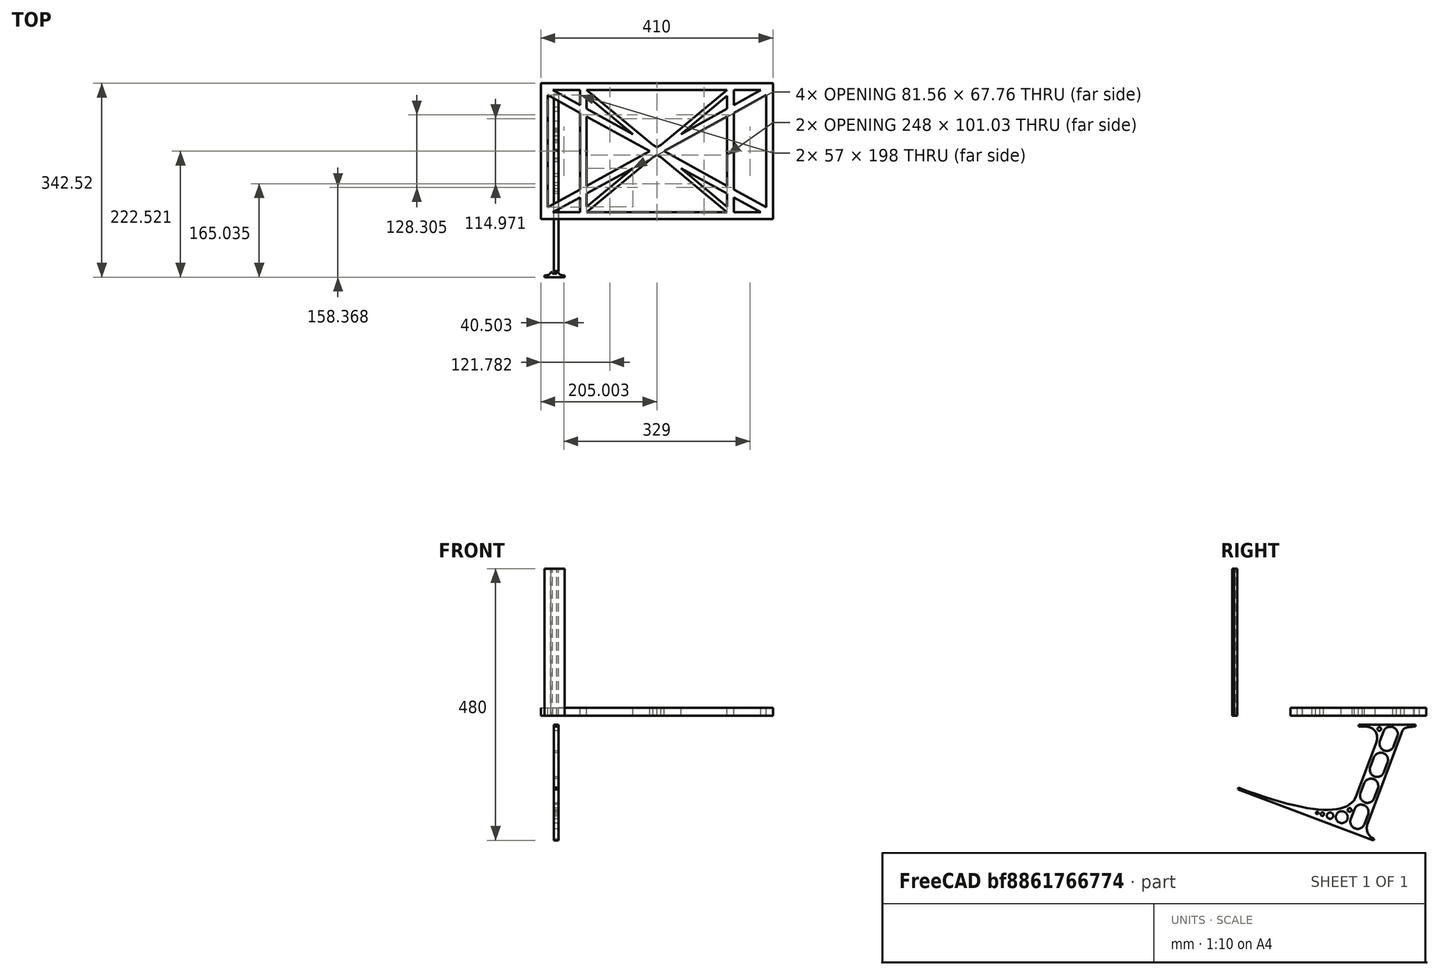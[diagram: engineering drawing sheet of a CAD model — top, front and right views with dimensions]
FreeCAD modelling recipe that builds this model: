
FCSTD DOCUMENT  (FreeCAD 0.19R0.19.2)
Label: laptopStand053
License: All rights reserved
LicenseURL: http://en.wikipedia.org/wiki/All_rights_reserved
objects: Sketcher::SketchObject×3, Part::Extrusion×3
note: 6 computed .brp shape members not serialized (recipe doc carries the construction recipe); baked Part::Feature solids carry a one-line shape summary decoded from their .brp

FEATURE [Sketcher::SketchObject] Sketch
  FullyConstrained = true
  sketch-geometry (92):
    g0: LineSegment StartX=-22.9272 StartY=136.221 StartZ=0 EndX=387.073 EndY=136.221 EndZ=0
    g1: LineSegment StartX=-22.9272 StartY=-103.779 StartZ=0 EndX=387.073 EndY=-103.779 EndZ=0
    g2: LineSegment StartX=375.073 StartY=115.221 StartZ=0 EndX=318.073 EndY=83.9235 EndZ=0
    g3: LineSegment StartX=-10.9272 StartY=-82.7794 StartZ=0 EndX=46.0728 EndY=-51.4823 EndZ=0
    g4: LineSegment StartX=-1.92719 StartY=124.221 StartZ=0 EndX=46.0728 EndY=97.8651 EndZ=0
    g5: LineSegment StartX=366.073 StartY=-91.7794 StartZ=0 EndX=318.073 EndY=-65.424 EndZ=0
    g6: LineSegment StartX=-10.9272 StartY=115.221 StartZ=0 EndX=-10.9272 EndY=-82.7794 EndZ=0
    g7: LineSegment StartX=375.073 StartY=-82.7794 StartZ=0 EndX=375.073 EndY=115.221 EndZ=0
    g8: LineSegment StartX=-1.92719 StartY=-91.7794 StartZ=0 EndX=46.0728 EndY=-91.7794 EndZ=0
    g9: LineSegment StartX=318.073 StartY=124.221 StartZ=0 EndX=366.073 EndY=124.221 EndZ=0
    g10: LineSegment StartX=306.073 StartY=-81.8102 StartZ=0 EndX=224.513 EndY=-14.0532 EndZ=0
    g11: LineSegment StartX=58.0728 StartY=114.251 StartZ=0 EndX=139.632 EndY=46.4944 EndZ=0
    g12: LineSegment StartX=306.073 StartY=124.221 StartZ=0 EndX=189.124 EndY=27.0628 EndZ=0
    g13: LineSegment StartX=58.0728 StartY=-91.7794 StartZ=0 EndX=175.022 EndY=5.37834 EndZ=0
    g14: LineSegment StartX=46.0728 StartY=124.221 StartZ=0 EndX=46.0728 EndY=97.8651 EndZ=0
    g15: LineSegment StartX=58.0728 StartY=-81.8102 StartZ=0 EndX=58.0728 EndY=-58.8351 EndZ=0
    g16: LineSegment StartX=318.073 StartY=124.221 StartZ=0 EndX=318.073 EndY=97.8651 EndZ=0
    g17: LineSegment StartX=306.073 StartY=114.251 StartZ=0 EndX=306.073 EndY=91.2763 EndZ=0
    g18: LineSegment StartX=224.513 StartY=46.4944 StartZ=0 EndX=306.073 EndY=114.251 EndZ=0
    g19: LineSegment StartX=175.022 StartY=27.0628 StartZ=0 EndX=58.0728 EndY=124.221 EndZ=0
    g20: LineSegment StartX=169.377 StartY=16.2206 StartZ=0 EndX=58.0728 EndY=77.3346 EndZ=0
    g21: LineSegment StartX=139.632 StartY=-14.0532 StartZ=0 EndX=58.0728 EndY=-81.8102 EndZ=0
    g22: LineSegment StartX=194.768 StartY=16.2206 StartZ=0 EndX=306.073 EndY=-44.8935 EndZ=0
    g23: LineSegment StartX=224.513 StartY=46.4944 StartZ=0 EndX=306.073 EndY=91.2763 EndZ=0
    g24: LineSegment StartX=139.632 StartY=-14.0532 StartZ=0 EndX=58.0728 EndY=-58.8351 EndZ=0
    g25: LineSegment StartX=189.124 StartY=5.37834 StartZ=0 EndX=306.073 EndY=-91.7794 EndZ=0
    g26: LineSegment StartX=306.073 StartY=77.3346 StartZ=0 EndX=306.073 EndY=-44.8935 EndZ=0
    g27: LineSegment StartX=318.073 StartY=83.9235 StartZ=0 EndX=318.073 EndY=-51.4823 EndZ=0
    g28: LineSegment StartX=318.073 StartY=97.8651 StartZ=0 EndX=366.073 EndY=124.221 EndZ=0
    g29: LineSegment StartX=306.073 StartY=77.3346 StartZ=0 EndX=194.768 EndY=16.2206 EndZ=0
    g30: LineSegment StartX=306.073 StartY=-58.8351 StartZ=0 EndX=224.513 EndY=-14.0532 EndZ=0
    g31: LineSegment StartX=306.073 StartY=-58.8351 StartZ=0 EndX=306.073 EndY=-81.8102 EndZ=0
    g32: LineSegment StartX=318.073 StartY=-51.4823 StartZ=0 EndX=375.073 EndY=-82.7794 EndZ=0
    g33: LineSegment StartX=318.073 StartY=-65.424 StartZ=0 EndX=318.073 EndY=-91.7794 EndZ=0
    g34: LineSegment StartX=318.073 StartY=-91.7794 StartZ=0 EndX=366.073 EndY=-91.7794 EndZ=0
    g35: LineSegment StartX=58.0728 StartY=-44.8935 StartZ=0 EndX=58.0728 EndY=77.3346 EndZ=0
    g36: LineSegment StartX=46.0728 StartY=-65.424 StartZ=0 EndX=-1.92719 EndY=-91.7794 EndZ=0
    g37: LineSegment StartX=46.0728 StartY=-65.424 StartZ=0 EndX=46.0728 EndY=-91.7794 EndZ=0
    g38: LineSegment StartX=58.0728 StartY=-44.8935 StartZ=0 EndX=169.377 EndY=16.2206 EndZ=0
    g39: LineSegment StartX=58.0728 StartY=91.2763 StartZ=0 EndX=58.0728 EndY=114.251 EndZ=0
    g40: LineSegment StartX=46.0728 StartY=83.9235 StartZ=0 EndX=46.0728 EndY=-51.4823 EndZ=0
    g41: LineSegment StartX=46.0728 StartY=124.221 StartZ=0 EndX=-1.92719 EndY=124.221 EndZ=0
    g42: LineSegment StartX=58.0728 StartY=91.2763 StartZ=0 EndX=139.632 EndY=46.4944 EndZ=0
    g43: LineSegment StartX=46.0728 StartY=83.9235 StartZ=0 EndX=-10.9272 EndY=115.221 EndZ=0
    g44: LineSegment StartX=-22.9272 StartY=136.221 StartZ=0 EndX=-42.9272 EndY=136.221 EndZ=0
    g45: LineSegment StartX=387.073 StartY=136.221 StartZ=0 EndX=407.073 EndY=136.221 EndZ=0
    g46: LineSegment StartX=-42.9272 StartY=136.221 StartZ=0 EndX=-42.9272 EndY=-103.779 EndZ=0
    g47: LineSegment StartX=-22.9272 StartY=-103.779 StartZ=0 EndX=-42.9272 EndY=-103.779 EndZ=0
    g48: LineSegment StartX=407.073 StartY=136.221 StartZ=0 EndX=407.073 EndY=-103.779 EndZ=0
    g49: LineSegment StartX=387.073 StartY=-103.779 StartZ=0 EndX=407.073 EndY=-103.779 EndZ=0
    g50: LineSegment StartX=179.022 StartY=27.0628 StartZ=0 EndX=179.022 EndY=124.221 EndZ=0
    g51: LineSegment StartX=185.124 StartY=27.0628 StartZ=0 EndX=185.124 EndY=124.221 EndZ=0
    g52: ArcOfCircle CenterX=-26.9272 CenterY=22.1087 CenterZ=0 NormalX=0 NormalY=0 NormalZ=1 AngleXU=0 Radius=8 StartAngle=1e-16 EndAngle=3.14159
    g53: ArcOfCircle CenterX=-26.9272 CenterY=-83.7794 CenterZ=0 NormalX=0 NormalY=0 NormalZ=1 AngleXU=0 Radius=8 StartAngle=3.14159 EndAngle=6.28319
    g54: LineSegment StartX=-34.9272 StartY=22.1087 StartZ=0 EndX=-34.9272 EndY=-83.7794 EndZ=0
    g55: LineSegment StartX=-18.9272 StartY=22.1087 StartZ=0 EndX=-18.9272 EndY=-83.7794 EndZ=0
    g56: LineSegment StartX=185.124 StartY=-91.7794 StartZ=0 EndX=306.073 EndY=-91.7794 EndZ=0
    g57: LineSegment StartX=179.022 StartY=-91.7794 StartZ=0 EndX=58.0728 EndY=-91.7794 EndZ=0
    g58: LineSegment StartX=306.073 StartY=124.221 StartZ=0 EndX=185.124 EndY=124.221 EndZ=0
    g59: LineSegment StartX=179.022 StartY=124.221 StartZ=0 EndX=58.0728 EndY=124.221 EndZ=0
    g60: ArcOfCircle CenterX=391.073 CenterY=22.1087 CenterZ=0 NormalX=0 NormalY=0 NormalZ=1 AngleXU=0 Radius=8 StartAngle=-4.4e-15 EndAngle=3.14159
    g61: LineSegment StartX=399.073 StartY=22.1087 StartZ=0 EndX=399.073 EndY=-83.7794 EndZ=0
    g62: LineSegment StartX=383.073 StartY=22.1087 StartZ=0 EndX=383.073 EndY=-83.7794 EndZ=0
    g63: ArcOfCircle CenterX=391.073 CenterY=-83.7794 CenterZ=0 NormalX=0 NormalY=0 NormalZ=1 AngleXU=0 Radius=8 StartAngle=3.14159 EndAngle=6.28319
    g64: Circle CenterX=175.022 CenterY=27.0628 CenterZ=0 NormalX=0 NormalY=0 NormalZ=1 AngleXU=0 Radius=1
    g65: Circle CenterX=179.022 CenterY=24.8665 CenterZ=0 NormalX=0 NormalY=0 NormalZ=1 AngleXU=0 Radius=1
    g66: Circle CenterX=179.022 CenterY=27.0628 CenterZ=0 NormalX=0 NormalY=0 NormalZ=1 AngleXU=0 Radius=1
    g67: BSplineCurve PolesCount=3 KnotsCount=2 Degree=2 IsPeriodic=0
    g68: GeomPoint X=175.022 Y=27.0628 Z=0
    g69: GeomPoint X=179.022 Y=27.0628 Z=0
    g70: Circle CenterX=189.124 CenterY=27.0628 CenterZ=0 NormalX=0 NormalY=0 NormalZ=1 AngleXU=0 Radius=1
    g71: Circle CenterX=185.124 CenterY=24.8665 CenterZ=0 NormalX=0 NormalY=0 NormalZ=1 AngleXU=0 Radius=1
    g72: Circle CenterX=185.124 CenterY=27.0628 CenterZ=0 NormalX=0 NormalY=0 NormalZ=1 AngleXU=0 Radius=1
    g73: BSplineCurve PolesCount=3 KnotsCount=2 Degree=2 IsPeriodic=0
    g74: GeomPoint X=189.124 Y=27.0628 Z=0
    g75: GeomPoint X=185.124 Y=27.0628 Z=0
    g76: Circle CenterX=175.022 CenterY=5.37834 CenterZ=0 NormalX=0 NormalY=0 NormalZ=1 AngleXU=0 Radius=1
    g77: Circle CenterX=179.022 CenterY=7.57463 CenterZ=0 NormalX=0 NormalY=0 NormalZ=1 AngleXU=0 Radius=1
    g78: Circle CenterX=179.022 CenterY=5.34704 CenterZ=0 NormalX=0 NormalY=0 NormalZ=1 AngleXU=0 Radius=1
    g79: BSplineCurve PolesCount=3 KnotsCount=2 Degree=2 IsPeriodic=0
    g80: GeomPoint X=175.022 Y=5.37834 Z=0
    g81: GeomPoint X=179.022 Y=5.34704 Z=0
    g82: Circle CenterX=189.124 CenterY=5.37834 CenterZ=0 NormalX=0 NormalY=0 NormalZ=1 AngleXU=0 Radius=1
    g83: Circle CenterX=185.124 CenterY=7.57463 CenterZ=0 NormalX=0 NormalY=0 NormalZ=1 AngleXU=0 Radius=1
    g84: Circle CenterX=185.124 CenterY=5.34704 CenterZ=0 NormalX=0 NormalY=0 NormalZ=1 AngleXU=0 Radius=1
    g85: BSplineCurve PolesCount=3 KnotsCount=2 Degree=2 IsPeriodic=0
    g86: GeomPoint X=189.124 Y=5.37834 Z=0
    g87: GeomPoint X=185.124 Y=5.34704 Z=0
    g88: LineSegment StartX=179.022 StartY=5.34704 StartZ=0 EndX=179.022 EndY=-91.7794 EndZ=0
    g89: LineSegment StartX=185.124 StartY=-91.7794 StartZ=0 EndX=185.124 EndY=5.34704 EndZ=0
    g90: LineSegment StartX=179.022 StartY=124.221 StartZ=0 EndX=177.022 EndY=124.221 EndZ=0
    g91: LineSegment StartX=179.022 StartY=124.221 StartZ=0 EndX=179.022 EndY=122.221 EndZ=0
  constraints (183):
    c: Horizontal(g0)
    c: Distance(g0) = 410
    c: Horizontal(g1)
    c: Block(g0)
    c: Horizontal(g8)
    c: Horizontal(g9)
    c: Tangent(g5,g20)
    c: PointOnObject(g20,g3)
    c: PointOnObject(g22,g2)
    c: Coincident(g42,g11)
    c: Coincident(g18,g23)
    c: Coincident(g24,g21)
    c: Coincident(g30,g10)
    c: Coincident(g18,g17)
    c: Tangent(g17,g26)
    c: Tangent(g16,g27)
    c: Coincident(g23,g17)
    c: Tangent(g23,g28)
    c: Coincident(g2,g27)
    c: Coincident(g29,g26)
    c: Tangent(g2,g29)
    c: Coincident(g31,g10)
    c: Tangent(g5,g30)
    c: Tangent(g26,g31)
    c: Coincident(g22,g26)
    c: Tangent(g22,g32)
    c: Coincident(g27,g32)
    c: Coincident(g33,g5)
    c: Tangent(g27,g33)
    c: Coincident(g21,g15)
    c: Tangent(g15,g35)
    c: Coincident(g24,g15)
    c: Tangent(g24,g36)
    c: Coincident(g37,g36)
    c: Tangent(g14,g37)
    c: Coincident(g3,g40)
    c: Coincident(g38,g35)
    c: Tangent(g3,g38)
    c: Tangent(g35,g39)
    c: Tangent(g14,g40)
    c: Coincident(g11,g39)
    c: Coincident(g4,g14)
    c: Coincident(g42,g39)
    c: Tangent(g4,g42)
    c: Coincident(g20,g35)
    c: Coincident(g43,g40)
    c: Tangent(g20,g43)
    c: Block(g19)
    c: Block(g12)
    c: Block(g16)
    c: Block(g28)
    c: Block(g2)
    c: Block(g32)
    c: Block(g7)
    c: Block(g30)
    c: Block(g31)
    c: Block(g5)
    c: Block(g33)
    c: Block(g18)
    c: Block(g25)
    c: Block(g13)
    c: Block(g24)
    c: Block(g21)
    c: Block(g37)
    c: Block(g36)
    c: Block(g3)
    c: Block(g6)
    c: Block(g43)
    c: Block(g4)
    c: Block(g14)
    c: Block(g11)
    c: Block(g39)
    c: Block(g29)
    c: Block(g26)
    c: Block(g20)
    c: Block(g38)
    c: Block(g41)
    c: Block(g9)
    c: Block(g34)
    c: Block(g8)
    c: Horizontal(g44)
    c: Distance(g44) = 20
    c: Coincident(g45,g0)
    c: Horizontal(g45)
    c: Distance(g45) = 20
    c: Coincident(g46,g44)
    c: Vertical(g46)
    c: Horizontal(g47)
    c: Coincident(g47,g46)
    c: Coincident(g48,g45)
    c: Vertical(g48)
    c: Coincident(g49,g1)
    c: Horizontal(g49)
    c: Coincident(g49,g48)
    c: Block(g48)
    c: Block(g47)
    c: Block(g46)
    c: Block(g1)
    c: Vertical(g50)
    c: Vertical(g51)
    c: Block(g50)
    c: Block(g51)
    c: Tangent(g52,g55) = 1.5708
    c: Tangent(g52,g54) = -1.5708
    c: Tangent(g54,g53) = -1.5708
    c: Tangent(g55,g53) = 1.5708
    c: Vertical(g54)
    c: Equal(g52,g53)
    c: Block(g55)
    c: Block(g54)
    c: Coincident(g56,g25)
    c: Horizontal(g56)
    c: Coincident(g57,g13)
    c: Horizontal(g57)
    c: Coincident(g58,g12)
    c: Coincident(g58,g51)
    c: Horizontal(g58)
    c: Coincident(g59,g50)
    c: Coincident(g59,g19)
    c: Horizontal(g59)
    c: Distance(g49) = 20
    c: Distance(g1) = 410
    c: Tangent(g60,g61) = 1.5708
    c: Tangent(g61,g63) = 1.5708
    c: Equal(g60,g63)
    c: Coincident(g62,g60)
    c: Coincident(g62,g63)
    c: Block(g61)
    c: Block(g62)
    c: Block(g22)
    c: Coincident(g67,g19)
    c: Weight(g64) = 1
    c: Equal(g64,g65)
    c: Equal(g64,g66)
    c: Coincident(g67,g50)
    c: InternalAlignment(g64,g67)
    c: InternalAlignment(g65,g67)
    c: InternalAlignment(g66,g67)
    c: InternalAlignment(g68,g67)
    c: InternalAlignment(g69,g67)
    c: Coincident(g73,g12)
    c: Weight(g70) = 1
    c: Equal(g70,g71)
    c: Equal(g70,g72)
    c: Coincident(g73,g51)
    c: InternalAlignment(g70,g73)
    c: InternalAlignment(g71,g73)
    c: InternalAlignment(g72,g73)
    c: InternalAlignment(g74,g73)
    c: InternalAlignment(g75,g73)
    c: Block(g73)
    c: Block(g67)
    c: Coincident(g79,g13)
    c: Weight(g76) = 1
    c: Equal(g76,g77)
    c: Equal(g76,g78)
    c: InternalAlignment(g76,g79)
    c: InternalAlignment(g77,g79)
    c: InternalAlignment(g78,g79)
    c: InternalAlignment(g80,g79)
    c: InternalAlignment(g81,g79)
    c: Weight(g82) = 1
    c: Equal(g82,g83)
    c: Equal(g82,g84)
    c: InternalAlignment(g82,g85)
    c: InternalAlignment(g83,g85)
    c: InternalAlignment(g84,g85)
    c: InternalAlignment(g86,g85)
    c: InternalAlignment(g87,g85)
    c: Block(g85)
    c: Block(g79)
    c: Coincident(g88,g79)
    c: Coincident(g88,g57)
    c: Vertical(g88)
    c: Coincident(g89,g56)
    c: Coincident(g89,g85)
    c: Vertical(g89)
    c: Horizontal(g90)
    c: Distance(g90) = 2
    c: Coincident(g90,g50)
    c: Distance(g91) = 2
    c: Vertical(g91)
    c: Coincident(g91,g50)
FEATURE [Sketcher::SketchObject] Sketch001
  FullyConstrained = true
  MapMode = 4
  Placement = pos=(0,0,0) rot=(0.57735,0.57735,0.57735;2.0944rad)
  Support = -> [Sketch]
  sketch-geometry (46):
    g0: BSplineCurve PolesCount=3 KnotsCount=2 Degree=2 IsPeriodic=0
    g1: ArcOfCircle CenterX=73.122 CenterY=-32.2909 CenterZ=0 NormalX=0 NormalY=0 NormalZ=1 AngleXU=0 Radius=13 StartAngle=5.92268 EndAngle=9.06428
    g2: ArcOfCircle CenterX=66.7816 CenterY=-49.1439 CenterZ=0 NormalX=0 NormalY=0 NormalZ=1 AngleXU=0 Radius=13 StartAngle=2.78068 EndAngle=5.92131
    g3: ArcOfCircle CenterX=55.9263 CenterY=-78.1807 CenterZ=0 NormalX=0 NormalY=0 NormalZ=1 AngleXU=0 Radius=13 StartAngle=5.92268 EndAngle=9.06428
    g4: ArcOfCircle CenterX=49.5884 CenterY=-95.0342 CenterZ=0 NormalX=0 NormalY=0 NormalZ=1 AngleXU=0 Radius=13 StartAngle=2.78068 EndAngle=5.92131
    g5: ArcOfCircle CenterX=38.7206 CenterY=-124.067 CenterZ=0 NormalX=0 NormalY=0 NormalZ=1 AngleXU=0 Radius=13 StartAngle=5.92268 EndAngle=9.06428
    g6: ArcOfCircle CenterX=32.3875 CenterY=-140.92 CenterZ=0 NormalX=0 NormalY=0 NormalZ=1 AngleXU=0 Radius=13 StartAngle=2.78068 EndAngle=5.92131
    g7: ArcOfCircle CenterX=21.4715 CenterY=-169.934 CenterZ=0 NormalX=0 NormalY=0 NormalZ=1 AngleXU=0 Radius=13 StartAngle=5.92268 EndAngle=9.06428
    g8: ArcOfCircle CenterX=15.1336 CenterY=-186.787 CenterZ=0 NormalX=0 NormalY=0 NormalZ=1 AngleXU=0 Radius=13 StartAngle=2.78068 EndAngle=5.92131
    g9-g12: Circle x4 (B-spline internal-alignment scaffolding for g13; pole/knot coordinates omitted)
    g13: BSplineCurve PolesCount=4 KnotsCount=2 Degree=3 IsPeriodic=0
    g14: GeomPoint X=28.8094 Y=-19.0875 Z=0
    g15: GeomPoint X=47.0443 Y=-50.4712 Z=0
    g16: Circle CenterX=53.5586 CenterY=-23.2695 CenterZ=0 NormalX=0 NormalY=0 NormalZ=1 AngleXU=0 Radius=3.24518
    g17: Circle CenterX=-195.441 CenterY=-127.082 CenterZ=0 NormalX=0 NormalY=0 NormalZ=1 AngleXU=0 Radius=1
    g18: Circle CenterX=-8.24091 CenterY=-197.481 CenterZ=0 NormalX=0 NormalY=0 NormalZ=1 AngleXU=0 Radius=1
    g19: Circle CenterX=12.8789 CenterY=-141.321 CenterZ=0 NormalX=0 NormalY=0 NormalZ=1 AngleXU=0 Radius=1
    g20: BSplineCurve PolesCount=3 KnotsCount=2 Degree=2 IsPeriodic=0
    g21: GeomPoint X=-195.441 Y=-127.082 Z=0
    g22: GeomPoint X=12.8789 Y=-141.321 Z=0
    g23: Circle CenterX=-12.8016 CenterY=-179.036 CenterZ=0 NormalX=0 NormalY=0 NormalZ=1 AngleXU=0 Radius=10.5072
    g24: Circle CenterX=0.933922 CenterY=-166.43 CenterZ=0 NormalX=0 NormalY=0 NormalZ=1 AngleXU=0 Radius=3.26661
    g25: Circle CenterX=-33.5518 CenterY=-176.44 CenterZ=0 NormalX=0 NormalY=0 NormalZ=1 AngleXU=0 Radius=5.64388
    g26: Circle CenterX=-47.2366 CenterY=-173.859 CenterZ=0 NormalX=0 NormalY=0 NormalZ=1 AngleXU=0 Radius=3.01653
    g27: Circle CenterX=-56.2595 CenterY=-171.456 CenterZ=0 NormalX=0 NormalY=0 NormalZ=1 AngleXU=0 Radius=2.12826
    g28: ArcOfCircle CenterX=51.2151 CenterY=-198.473 CenterZ=0 NormalX=0 NormalY=0 NormalZ=1 AngleXU=0 Radius=20 StartAngle=2.78189 EndAngle=4.35269
    g29: LineSegment StartX=32.4951 StartY=-191.433 StartZ=0 EndX=94.6577 EndY=-26.1351 EndZ=0
    g30: LineSegment StartX=43.1192 StartY=-220.001 StartZ=0 EndX=-196.497 EndY=-129.89 EndZ=0
    g31: LineSegment StartX=43.1192 StartY=-220.001 StartZ=0 EndX=44.1752 EndY=-217.193 EndZ=0
    g32: LineSegment StartX=117.223 StartY=-19.0875 StartZ=0 EndX=117.223 EndY=-16.0875 EndZ=0
    g33: LineSegment StartX=117.223 StartY=-16.0875 StartZ=0 EndX=17.2232 EndY=-16.0875 EndZ=0
    g34: LineSegment StartX=17.2232 StartY=-16.0875 StartZ=0 EndX=17.2232 EndY=-19.0875 EndZ=0
    g35: LineSegment StartX=28.8094 StartY=-19.0875 StartZ=0 EndX=17.2232 EndY=-19.0875 EndZ=0
    g36: LineSegment StartX=47.0443 StartY=-50.4712 StartZ=0 EndX=12.8789 EndY=-141.321 EndZ=0
    g37: LineSegment StartX=-195.441 StartY=-127.082 StartZ=0 EndX=-196.497 EndY=-129.89 EndZ=0
    g38: LineSegment StartX=85.2864 StartY=-36.8765 StartZ=0 EndX=78.9396 EndY=-53.7463 EndZ=0
    g39: LineSegment StartX=60.9577 StartY=-27.7052 StartZ=0 EndX=54.6191 EndY=-44.5532 EndZ=0
    g40: LineSegment StartX=68.0907 StartY=-82.7664 StartZ=0 EndX=61.7465 EndY=-99.6365 EndZ=0
    g41: LineSegment StartX=43.7619 StartY=-73.595 StartZ=0 EndX=37.426 EndY=-90.4435 EndZ=0
    g42: LineSegment StartX=50.885 StartY=-128.652 StartZ=0 EndX=44.5456 EndY=-145.522 EndZ=0
    g43: LineSegment StartX=26.5562 StartY=-119.481 StartZ=0 EndX=20.2251 EndY=-136.329 EndZ=0
    g44: LineSegment StartX=9.3071 StartY=-165.349 StartZ=0 EndX=2.97115 EndY=-182.197 EndZ=0
    g45: LineSegment StartX=33.6358 StartY=-174.52 StartZ=0 EndX=27.2917 EndY=-191.39 EndZ=0
  constraints (70):
    c: Block(g0)
    c: Block(g1)
    c: Block(g2)
    c: Block(g4)
    c: Block(g3)
    c: Block(g6)
    c: Block(g5)
    c: Block(g8)
    c: Block(g7)
    c: Weight(g9) = 1
    c: Equal(g9,g10)
    c: Equal(g9,g11)
    c: Equal(g9,g12)
    c: InternalAlignment(g9-g12 -> g13) x4
    c: InternalAlignment(g14,g13)
    c: InternalAlignment(g15,g13)
    c: Block(g16)
    c: Weight(g17) = 1
    c: Equal(g17,g18)
    c: Equal(g17,g19)
    c: InternalAlignment(g17,g20)
    c: InternalAlignment(g18,g20)
    c: InternalAlignment(g19,g20)
    c: InternalAlignment(g21,g20)
    c: InternalAlignment(g22,g20)
    c: Block(g20)
    c: Block(g23)
    c: Block(g24)
    c: Block(g25)
    c: Block(g26)
    c: Block(g27)
    c: Block(g28)
    c: Coincident(g29,g28)
    c: Coincident(g29,g0)
    c: Block(g13)
    c: Coincident(g31,g30)
    c: Coincident(g31,g28)
    c: Block(g31)
    c: Coincident(g32,g0)
    c: Vertical(g32)
    c: Coincident(g33,g32)
    c: Horizontal(g33)
    c: Coincident(g34,g33)
    c: Vertical(g34)
    c: Block(g33)
    c: Coincident(g35,g13)
    c: Coincident(g35,g34)
    c: Horizontal(g35)
    c: Coincident(g36,g13)
    c: Coincident(g36,g20)
    c: Coincident(g37,g20)
    c: Coincident(g37,g30)
    c: Block(g30)
    c: Coincident(g38,g1)
    c: Coincident(g38,g2)
    c: Coincident(g39,g1)
    c: Coincident(g39,g2)
    c: Coincident(g40,g3)
    c: Coincident(g40,g4)
    c: Coincident(g41,g3)
    c: Coincident(g41,g4)
    c: Coincident(g42,g5)
    c: Coincident(g42,g6)
    c: Coincident(g43,g5)
    c: Coincident(g43,g6)
    c: Coincident(g44,g7)
    c: Coincident(g44,g8)
    c: Coincident(g45,g7)
    c: Coincident(g45,g8)
    c: Distance(g30) = 256
FEATURE [Part::Extrusion] Extrude002
  Base = -> Sketch001
  Dir = (1,0,0)
  DirMode = 2
  FaceMakerClass = Part::FaceMakerBullseye
  LengthFwd = 8
  LengthRev = 0
  Solid = true
  Symmetric = false
FEATURE [Sketcher::SketchObject] Sketch002
  FullyConstrained = true
  sketch-geometry (20):
    g0: LineSegment StartX=-2.77179 StartY=-200.304 StartZ=0 EndX=5.22821 EndY=-200.304 EndZ=0
    g1: LineSegment StartX=5.22821 StartY=-200.304 StartZ=0 EndX=5.22821 EndY=-197.304 EndZ=0
    g2: LineSegment StartX=-2.77179 StartY=-200.304 StartZ=0 EndX=-2.77179 EndY=-197.304 EndZ=0
    g3: LineSegment StartX=5.22821 StartY=-197.304 StartZ=0 EndX=8.22821 EndY=-197.304 EndZ=0
    g4: LineSegment StartX=-2.77179 StartY=-197.304 StartZ=0 EndX=-5.77179 EndY=-197.304 EndZ=0
    g5: LineSegment StartX=19.2282 StartY=-203.304 StartZ=0 EndX=19.2282 EndY=-206.304 EndZ=0
    g6: LineSegment StartX=-16.7718 StartY=-203.304 StartZ=0 EndX=-16.7718 EndY=-206.304 EndZ=0
    g7: LineSegment StartX=-16.7718 StartY=-206.304 StartZ=0 EndX=19.2282 EndY=-206.304 EndZ=0
    g8: Circle CenterX=-16.7718 CenterY=-203.304 CenterZ=0 NormalX=0 NormalY=0 NormalZ=1 AngleXU=0 Radius=1
    g9: Circle CenterX=-5.77179 CenterY=-203.304 CenterZ=0 NormalX=0 NormalY=0 NormalZ=1 AngleXU=0 Radius=1
    g10: Circle CenterX=-5.77179 CenterY=-197.304 CenterZ=0 NormalX=0 NormalY=0 NormalZ=1 AngleXU=0 Radius=1
    g11: BSplineCurve PolesCount=3 KnotsCount=2 Degree=2 IsPeriodic=0
    g12: GeomPoint X=-16.7718 Y=-203.304 Z=0
    g13: GeomPoint X=-5.77179 Y=-197.304 Z=0
    g14: Circle CenterX=19.2282 CenterY=-203.304 CenterZ=0 NormalX=0 NormalY=0 NormalZ=1 AngleXU=0 Radius=1
    g15: Circle CenterX=8.22821 CenterY=-203.304 CenterZ=0 NormalX=0 NormalY=0 NormalZ=1 AngleXU=0 Radius=1
    g16: Circle CenterX=8.22821 CenterY=-197.304 CenterZ=0 NormalX=0 NormalY=0 NormalZ=1 AngleXU=0 Radius=1
    g17: BSplineCurve PolesCount=3 KnotsCount=2 Degree=2 IsPeriodic=0
    g18: GeomPoint X=19.2282 Y=-203.304 Z=0
    g19: GeomPoint X=8.22821 Y=-197.304 Z=0
  constraints (41):
    c: Horizontal(g0)
    c: Distance(g0) = 8
    c: Coincident(g1,g0)
    c: Vertical(g1)
    c: Distance(g1) = 3
    c: Coincident(g2,g0)
    c: Vertical(g2)
    c: Distance(g2) = 3
    c: Coincident(g3,g1)
    c: Horizontal(g3)
    c: Distance(g3) = 3
    c: Coincident(g4,g2)
    c: Horizontal(g4)
    c: Distance(g4) = 3
    c: Vertical(g5)
    c: Vertical(g6)
    c: Coincident(g7,g6)
    c: Coincident(g7,g5)
    c: Weight(g8) = 1
    c: Equal(g8,g9)
    c: Equal(g8,g10)
    c: Coincident(g11,g4)
    c: InternalAlignment(g8,g11)
    c: InternalAlignment(g9,g11)
    c: InternalAlignment(g10,g11)
    c: InternalAlignment(g12,g11)
    c: InternalAlignment(g13,g11)
    c: Coincident(g17,g5)
    c: Weight(g14) = 1
    c: Equal(g14,g15)
    c: Equal(g14,g16)
    c: Coincident(g17,g3)
    c: InternalAlignment(g14,g17)
    c: InternalAlignment(g15,g17)
    c: InternalAlignment(g16,g17)
    c: InternalAlignment(g18,g17)
    c: InternalAlignment(g19,g17)
    c: Block(g7)
    c: Block(g17)
    c: Block(g11)
    c: Block(g6)
FEATURE [Part::Extrusion] Extrude003
  Base = -> Sketch002
  Dir = (0,0,1)
  DirMode = 2
  FaceMakerClass = Part::FaceMakerBullseye
  LengthFwd = 260
  LengthRev = 0
  Solid = true
  Symmetric = false
FEATURE [Part::Extrusion] Extrude
  Base = -> Sketch
  Dir = (0,0,1)
  DirMode = 2
  FaceMakerClass = Part::FaceMakerBullseye
  LengthFwd = 14
  LengthRev = 0
  Solid = true
  Symmetric = false
